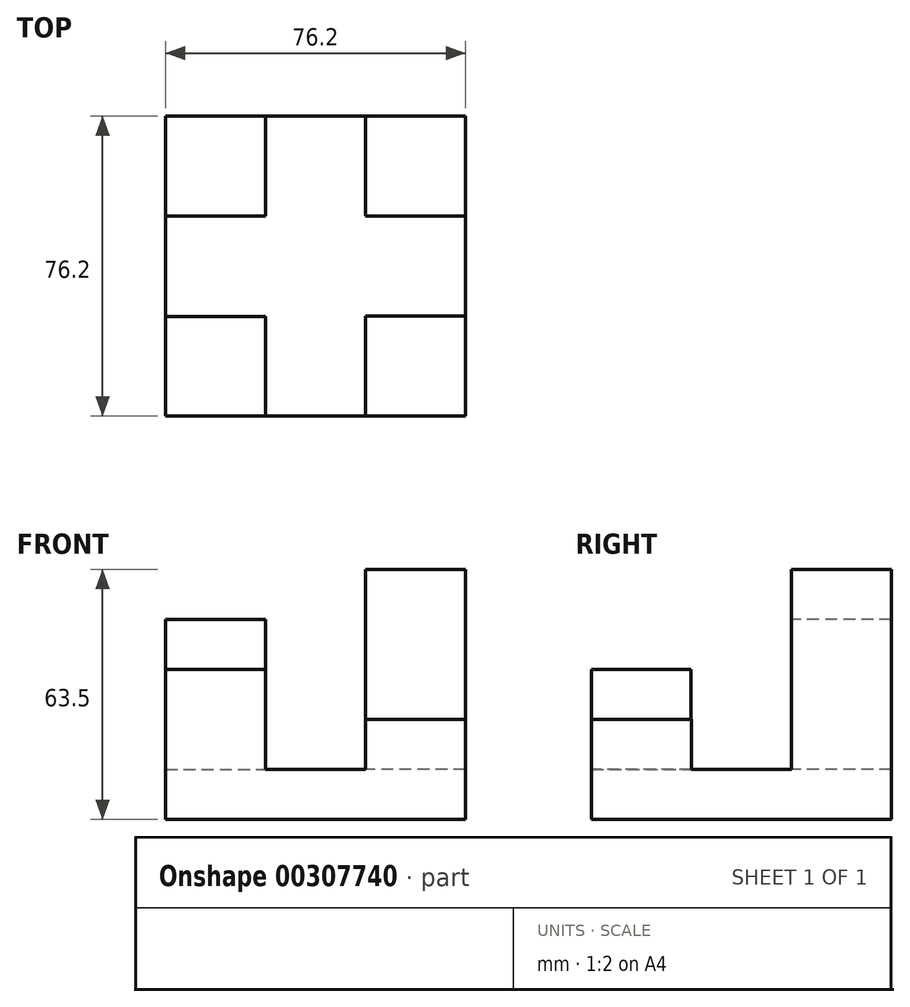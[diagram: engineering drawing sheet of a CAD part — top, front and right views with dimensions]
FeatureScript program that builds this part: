
annotation { "Feature Type Name" : "Feature", "Feature Type Description" : "" }
export const myFeature = defineFeature(function(context is Context, id is Id, definition is map)
    precondition{}
    {
        {
            var Q0;
            Q0=qCreatedBy(makeId("Top.planeOp"),FACE);
            var sketch = newSketch(context, id + "F0", { "sketchPlane" : qUnion([Q0])});
            skLineSegment(sketch, "E0", {"start": v(-42.12, -25.24) * mm, "end": v(34.08, -25.24) * mm});
            skLineSegment(sketch, "E1", {"start": v(34.08, -25.24) * mm, "end": v(34.08, 50.96) * mm});
            skLineSegment(sketch, "E2", {"start": v(34.08, 50.96) * mm, "end": v(-42.12, 50.96) * mm});
            skLineSegment(sketch, "E3", {"start": v(-42.12, 50.96) * mm, "end": v(-42.12, -25.24) * mm});
            skSolve(sketch);
        }
        {
            var Q0;
            Q0=makeQuery(id+"F0.imprint","IMPRINT",FACE,{"disambiguationData":[TD([[makeQuery(id+"F0.imprint","IMPRINT",EDGE,{"derivedFrom":sQuery(id+"F0.wireOp",EDGE,"E0")}),1.0]])]});
            extrude(context, id + "F1", {"entities" : qUnion([Q0]), "depth" : 12.7 * mm});
        }
        {
            var Q0;
            Q0=makeQuery(id+"F1.opExtrude","CAP_FACE",FACE,{"disambiguationData":[OSD([sQuery(id+"F0.wireOp",EDGE,"E0"),sQuery(id+"F0.wireOp",EDGE,"E1"),sQuery(id+"F0.wireOp",EDGE,"E2"),sQuery(id+"F0.wireOp",EDGE,"E3")])],"isStart":false});
            var sketch = newSketch(context, id + "F2", { "sketchPlane" : qUnion([Q0])});
            skLineSegment(sketch, "E4.bottom", {"start": v(-42.12, -25.24) * mm, "end": v(-16.72, -25.24) * mm});
            skLineSegment(sketch, "E4.top", {"start": v(-42.12, 0.16) * mm, "end": v(-16.72, 0.16) * mm});
            skLineSegment(sketch, "E4.left", {"start": v(-42.12, -25.24) * mm, "end": v(-42.12, 0.16) * mm});
            skLineSegment(sketch, "E4.right", {"start": v(-16.72, -25.24) * mm, "end": v(-16.72, 0.16) * mm});
            skLineSegment(sketch, "E5.bottom", {"start": v(34.08, -25.24) * mm, "end": v(8.68, -25.24) * mm});
            skLineSegment(sketch, "E5.top", {"start": v(34.08, 0.16) * mm, "end": v(8.68, 0.16) * mm});
            skLineSegment(sketch, "E5.left", {"start": v(34.08, -25.24) * mm, "end": v(34.08, 0.16) * mm});
            skLineSegment(sketch, "E5.right", {"start": v(8.68, -25.24) * mm, "end": v(8.68, 0.16) * mm});
            skLineSegment(sketch, "E6.bottom", {"start": v(-42.12, 50.96) * mm, "end": v(-16.72, 50.96) * mm});
            skLineSegment(sketch, "E6.top", {"start": v(-42.12, 25.56) * mm, "end": v(-16.72, 25.56) * mm});
            skLineSegment(sketch, "E6.left", {"start": v(-42.12, 50.96) * mm, "end": v(-42.12, 25.56) * mm});
            skLineSegment(sketch, "E6.right", {"start": v(-16.72, 50.96) * mm, "end": v(-16.72, 25.56) * mm});
            skLineSegment(sketch, "E7.bottom", {"start": v(34.08, 50.96) * mm, "end": v(8.68, 50.96) * mm});
            skLineSegment(sketch, "E7.top", {"start": v(34.08, 25.56) * mm, "end": v(8.68, 25.56) * mm});
            skLineSegment(sketch, "E7.left", {"start": v(34.08, 50.96) * mm, "end": v(34.08, 25.56) * mm});
            skLineSegment(sketch, "E7.right", {"start": v(8.68, 50.96) * mm, "end": v(8.68, 25.56) * mm});
            skSolve(sketch);
        }
        {
            var Q0;
            Q0=makeQuery(id+"F2.imprint","IMPRINT",FACE,{"disambiguationData":[TD([[makeQuery(id+"F2.imprint","IMPRINT",EDGE,{"derivedFrom":sQuery(id+"F2.wireOp",EDGE,"E7.bottom")}),1.0]])]});
            extrude(context, id + "F3", {"entities" : qUnion([Q0]), "operationType" : NewBodyOperationType.ADD, "depth" : 50.8 * mm});
        }
        {
            var Q0;
            Q0=makeQuery(id+"F1.opExtrude","CAP_FACE",FACE,{"disambiguationData":[OSD([sQuery(id+"F0.wireOp",EDGE,"E0"),sQuery(id+"F0.wireOp",EDGE,"E1"),sQuery(id+"F0.wireOp",EDGE,"E2"),sQuery(id+"F0.wireOp",EDGE,"E3")])],"isStart":false});
            var sketch = newSketch(context, id + "F4", { "sketchPlane" : qUnion([Q0])});
            skLineSegment(sketch, "E8.bottom", {"start": v(-42.12, 50.96) * mm, "end": v(-16.72, 50.96) * mm});
            skLineSegment(sketch, "E8.top", {"start": v(-42.12, 25.56) * mm, "end": v(-16.72, 25.56) * mm});
            skLineSegment(sketch, "E8.left", {"start": v(-42.12, 50.96) * mm, "end": v(-42.12, 25.56) * mm});
            skLineSegment(sketch, "E8.right", {"start": v(-16.72, 50.96) * mm, "end": v(-16.72, 25.56) * mm});
            skSolve(sketch);
        }
        {
            var Q0;
            Q0=makeQuery(id+"F4.imprint","IMPRINT",FACE,{"disambiguationData":[TD([[makeQuery(id+"F4.imprint","IMPRINT",EDGE,{"derivedFrom":sQuery(id+"F4.wireOp",EDGE,"E8.bottom")}),1.0]])]});
            extrude(context, id + "F5", {"entities" : qUnion([Q0]), "operationType" : NewBodyOperationType.ADD, "depth" : 38.1 * mm});
        }
        {
            var Q0;
            Q0=makeQuery(id+"F1.opExtrude","CAP_FACE",FACE,{"disambiguationData":[OSD([sQuery(id+"F0.wireOp",EDGE,"E0"),sQuery(id+"F0.wireOp",EDGE,"E1"),sQuery(id+"F0.wireOp",EDGE,"E2"),sQuery(id+"F0.wireOp",EDGE,"E3")])],"isStart":false});
            var sketch = newSketch(context, id + "F6", { "sketchPlane" : qUnion([Q0])});
            skLineSegment(sketch, "E9.bottom", {"start": v(-42.12, -25.24) * mm, "end": v(-16.71, -25.24) * mm});
            skLineSegment(sketch, "E9.top", {"start": v(-42.12, 0) * mm, "end": v(-16.71, 0) * mm});
            skLineSegment(sketch, "E9.left", {"start": v(-42.12, -25.24) * mm, "end": v(-42.12, 0) * mm});
            skLineSegment(sketch, "E9.right", {"start": v(-16.71, -25.24) * mm, "end": v(-16.71, 0) * mm});
            skSolve(sketch);
        }
        {
            var Q0;
            Q0=makeQuery(id+"F6.imprint","IMPRINT",FACE,{"disambiguationData":[TD([[makeQuery(id+"F6.imprint","IMPRINT",EDGE,{"derivedFrom":sQuery(id+"F6.wireOp",EDGE,"E9.bottom")}),1.0]])]});
            extrude(context, id + "F7", {"entities" : qUnion([Q0]), "operationType" : NewBodyOperationType.ADD, "depth" : 25.4 * mm});
        }
        {
            var Q0;
            Q0=makeQuery(id+"F1.opExtrude","CAP_FACE",FACE,{"disambiguationData":[OSD([sQuery(id+"F0.wireOp",EDGE,"E0"),sQuery(id+"F0.wireOp",EDGE,"E1"),sQuery(id+"F0.wireOp",EDGE,"E2"),sQuery(id+"F0.wireOp",EDGE,"E3")])],"isStart":false});
            var sketch = newSketch(context, id + "F8", { "sketchPlane" : qUnion([Q0])});
            skLineSegment(sketch, "E10", {"start": v(34.08, -25.24) * mm, "end": v(34.08, 0.16) * mm});
            skLineSegment(sketch, "E11", {"start": v(34.08, 0.16) * mm, "end": v(8.67, 0.16) * mm});
            skLineSegment(sketch, "E12", {"start": v(8.67, 0.16) * mm, "end": v(8.67, -25.24) * mm});
            skLineSegment(sketch, "E13", {"start": v(8.67, -25.24) * mm, "end": v(34.08, -25.24) * mm});
            skSolve(sketch);
        }
        {
            var Q0;
            Q0=makeQuery(id+"F8.imprint","IMPRINT",FACE,{"disambiguationData":[TD([[makeQuery(id+"F8.imprint","IMPRINT",EDGE,{"derivedFrom":sQuery(id+"F8.wireOp",EDGE,"E10")}),1.0]])]});
            extrude(context, id + "F9", {"entities" : qUnion([Q0]), "operationType" : NewBodyOperationType.ADD, "depth" : 12.7 * mm});
        }
    });
